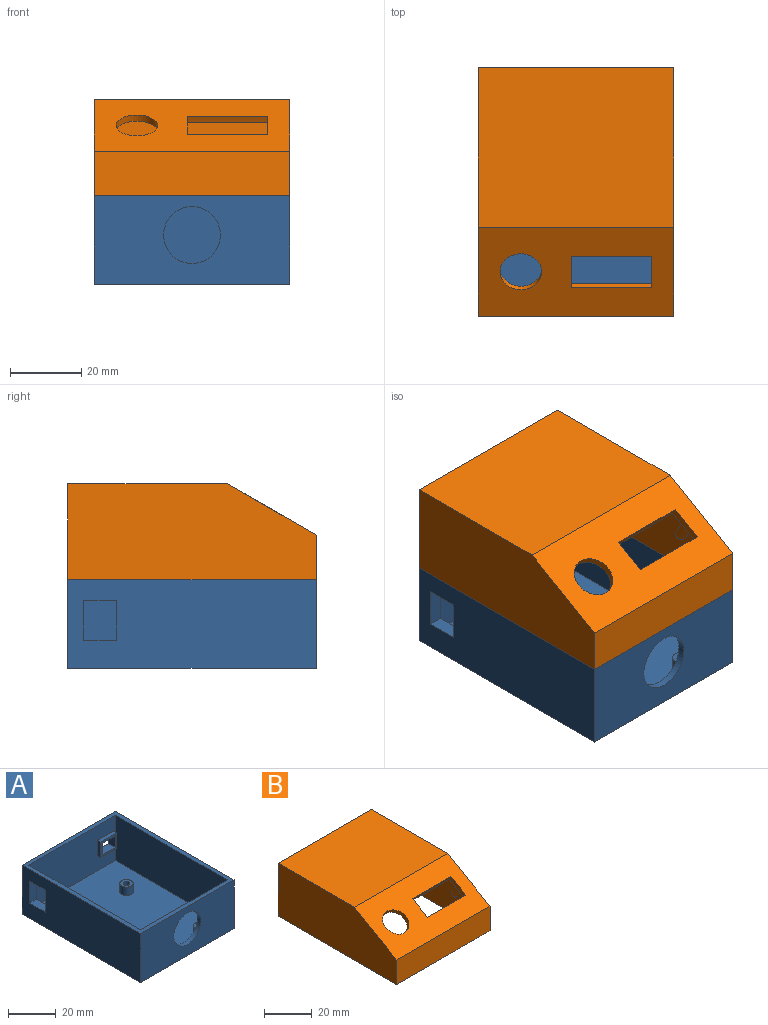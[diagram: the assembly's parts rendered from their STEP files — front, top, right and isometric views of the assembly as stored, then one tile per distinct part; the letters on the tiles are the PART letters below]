
ASSEMBLY  parts=2 mates=1
PART A: 46 faces, bbox 55x70x25 mm
  f0: plane 55x25mm, normal (0,1,0), area 1330.8mm2, adj f3,f4,f6,f9,f36,f37,f38,f39
  f1: plane 51x23mm, normal (0,-1,0), area 1098mm2, adj f2,f7,f9,f10,f40,f41,f42,f43
  f2: plane 66x23mm, normal (1,0,0), area 1370.2mm2, adj f1,f8,f9,f10,f31,f32,f33,f34
  f3: plane 70x25mm, normal (-1,0,0), area 1647mm2, adj f0,f5,f6,f9,f27,f28,f29,f30
  f4: plane 70x25mm, normal (1,0,0), area 1750mm2, adj f0,f5,f6,f9
  f5: plane 55x25mm, normal (0,-1,0), area 1173.9mm2, adj f3,f4,f6,f9,f45
  f6: plane 70x55mm, normal (0,0,-1), area 3850mm2, adj f0,f3,f4,f5
  f7: plane 66x23mm, normal (-1,0,0), area 1518mm2, adj f1,f8,f9,f10
  f8: plane 51x23mm, normal (0,1,0), area 971.9mm2, adj f2,f7,f9,f10,f45
  f9: plane 70x55mm, normal (0,0,1), area 484mm2, adj f0,f1,f2,f3,f4,f5,f7,f8
  f10: plane 66x51mm, normal (0,0,1), area 3271mm2, adj f1,f2,f7,f8,f12,f16,f20,f24
  f11: cylinder r=1.45mm len=4.25mm, axis (0,0,-1), area 38.7mm2, adj f13,f14
  f12: cylinder r=2.75mm len=5.5mm, axis (0,0,-1), area 73.4mm2, adj f10,f13
  f13: plane 5.5x5.5mm, normal (0,0,1), area 17.2mm2, adj f11,f12
  f14: plane 2.9x2.9mm, normal (0,0,1), area 6.6mm2, adj f11
  f15: cylinder r=1.45mm len=4.25mm, axis (0,0,-1), area 38.7mm2, adj f17,f18
  f16: cylinder r=2.75mm len=5.5mm, axis (0,0,-1), area 73.4mm2, adj f10,f17
  f17: plane 5.5x5.5mm, normal (0,0,1), area 17.2mm2, adj f15,f16
  f18: plane 2.9x2.9mm, normal (0,0,1), area 6.6mm2, adj f15
  f19: cylinder r=1.45mm len=4.25mm, axis (0,0,-1), area 38.7mm2, adj f21,f22
  f20: cylinder r=2.75mm len=5.5mm, axis (0,0,-1), area 73.4mm2, adj f10,f21
  f21: plane 5.5x5.5mm, normal (0,0,1), area 17.2mm2, adj f19,f20
  f22: plane 2.9x2.9mm, normal (0,0,1), area 6.6mm2, adj f19
  f23: cylinder r=1.45mm len=4.25mm, axis (0,0,-1), area 38.7mm2, adj f25,f26
  f24: cylinder r=2.75mm len=5.5mm, axis (0,0,-1), area 73.4mm2, adj f10,f25
  f25: plane 5.5x5.5mm, normal (0,0,1), area 17.2mm2, adj f23,f24
  f26: plane 2.9x2.9mm, normal (0,0,1), area 6.6mm2, adj f23
  f27: plane 11.2x4mm, normal (0,-1,0), area 44.8mm2, adj f3,f28,f30,f35
  f28: plane 9.2x4mm, normal (0,0,-1), area 36.8mm2, adj f3,f27,f29,f35
  f29: plane 11.2x4mm, normal (0,1,0), area 44.8mm2, adj f3,f28,f30,f35
  f30: plane 9.2x4mm, normal (0,0,1), area 36.8mm2, adj f3,f27,f29,f35
  f31: plane 11.2x2mm, normal (0,0,1), area 22.4mm2, adj f2,f32,f34,f35
  f32: plane 13.2x2mm, normal (0,-1,0), area 26.4mm2, adj f2,f31,f33,f35
  f33: plane 11.2x2mm, normal (0,0,-1), area 22.4mm2, adj f2,f32,f34,f35
  f34: plane 13.2x2mm, normal (0,1,0), area 26.4mm2, adj f2,f31,f33,f35
  f35: plane 13.2x11.2mm, normal (1,0,0), area 44.8mm2, adj f27,f28,f29,f30,f31,f32,f33,f34
  f36: plane 7.5x4mm, normal (0,0,1), area 30mm2, adj f0,f37,f39,f44
  f37: plane 5.9x4mm, normal (-1,0,0), area 23.6mm2, adj f0,f36,f38,f44
  f38: plane 7.5x4mm, normal (0,0,-1), area 30mm2, adj f0,f37,f39,f44
  f39: plane 5.9x4mm, normal (1,0,0), area 23.6mm2, adj f0,f36,f38,f44
  f40: plane 7.9x2mm, normal (-1,0,0), area 15.8mm2, adj f1,f41,f43,f44
  f41: plane 9.5x2mm, normal (0,0,-1), area 19mm2, adj f1,f40,f42,f44
  f42: plane 7.9x2mm, normal (1,0,0), area 15.8mm2, adj f1,f41,f43,f44
  f43: plane 9.5x2mm, normal (0,0,1), area 19mm2, adj f1,f40,f42,f44
  f44: plane 9.5x7.9mm, normal (0,-1,0), area 30.8mm2, adj f36,f37,f38,f39,f40,f41,f42,f43
  f45: cylinder r=8mm len=16mm, axis (0,-1,0), area 100.5mm2, adj f5,f8
PART B: 26 faces, bbox 55x70x27 mm
  f0: plane 55x25mm, normal (0,-0.5,0.87), area 1253.8mm2, adj f2,f3,f9,f12,f13,f14,f15,f16
  f1: plane 51x23.54mm, normal (0,0.5,-0.87), area 1037.8mm2, adj f4,f5,f6,f7,f13,f14,f15,f16
  f2: plane 70x27mm, normal (-1,0,0), area 1708.7mm2, adj f0,f8,f9,f11,f12
  f3: plane 70x27mm, normal (1,0,0), area 1708.8mm2, adj f0,f8,f9,f11,f12
  f4: plane 51x42.46mm, normal (0,0,-1), area 2165.6mm2, adj f1,f5,f7,f10
  f5: plane 66x25mm, normal (-1,0,0), area 1489.3mm2, adj f1,f4,f6,f10,f11
  f6: plane 51x11.35mm, normal (0,1,0), area 578.7mm2, adj f1,f5,f7,f11
  f7: plane 66x25mm, normal (1,0,0), area 1489.3mm2, adj f1,f4,f6,f10,f11
  f8: plane 55x27mm, normal (0,1,0), area 1485mm2, adj f2,f3,f11,f12
  f9: plane 55x12.5mm, normal (0,-1,0), area 687.5mm2, adj f0,f2,f3,f11
  f10: plane 51x25mm, normal (0,-1,0), area 1275mm2, adj f4,f5,f7,f11
  f11: plane 70x55mm, normal (0,0,-1), area 484mm2, adj f2,f3,f5,f6,f7,f8,f9,f10
  f12: plane 55x45mm, normal (0,0,1), area 2475mm2, adj f0,f2,f3,f8
  f13: plane 9.74x6.8mm, normal (-1,0,0), area 20.2mm2, adj f0,f1,f14,f16
  f14: plane 22.6x1.73mm, normal (0,-0.87,-0.5), area 45.2mm2, adj f0,f1,f13,f15
  f15: plane 9.74x6.8mm, normal (1,0,0), area 20.2mm2, adj f0,f1,f14,f16
  f16: plane 22.6x1.73mm, normal (0,0.87,0.5), area 45.2mm2, adj f0,f1,f13,f15
  f17: cylinder r=5.85mm len=11.7mm, axis (0,-0.5,0.87), area 73.5mm2, adj f0,f1
  f18: cylinder r=0.93mm len=6.33mm, axis (0,-0.5,0.87), area 36.3mm2, adj f20,f21
  f19: cylinder r=1.5mm len=6.91mm, axis (0,-0.5,0.87), area 58.9mm2, adj f1,f20
  f20: plane 3x2.6mm, normal (0,0.5,-0.87), area 4.4mm2, adj f18,f19
  f21: plane 1.85x1.6mm, normal (0,0.5,-0.87), area 2.7mm2, adj f18
  f22: cylinder r=0.93mm len=6.33mm, axis (0,-0.5,0.87), area 36.3mm2, adj f24,f25
  f23: cylinder r=1.5mm len=6.91mm, axis (0,-0.5,0.87), area 58.9mm2, adj f1,f24
  f24: plane 3x2.6mm, normal (0,0.5,-0.87), area 4.4mm2, adj f22,f23
  f25: plane 1.85x1.6mm, normal (0,0.5,-0.87), area 2.7mm2, adj f22
PLACE A t=(-0.18,-0.16,-12.58)mm
PLACE B t=(-0.18,-0.16,12.42)mm
MATE planar B.f11 <-> A.f9  axis (0,0,-1) through (-25.68,-33.16,12.42)mm
